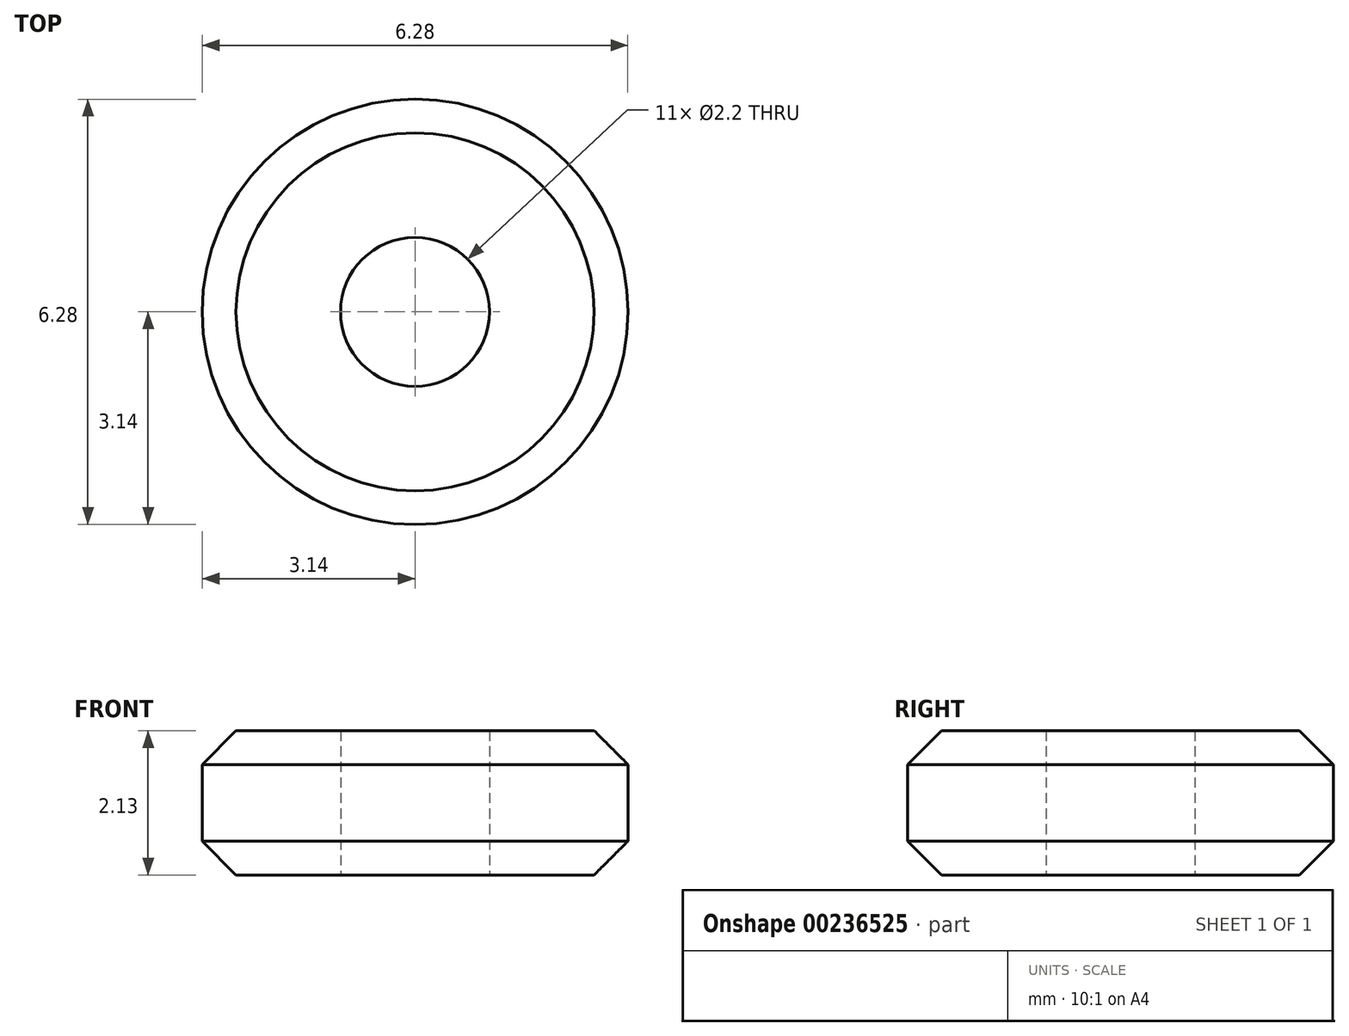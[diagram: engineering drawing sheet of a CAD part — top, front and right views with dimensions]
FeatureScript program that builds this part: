
annotation { "Feature Type Name" : "Feature", "Feature Type Description" : "" }
export const myFeature = defineFeature(function(context is Context, id is Id, definition is map)
    precondition{}
    {
        {
            assignVariable(context, id + "F0", {"name" : "scale", "anyValue" : 1 / 160});
        }
        {
            var Q0;
            Q0=qCreatedBy(makeId("Top.planeOp"),FACE);
            var sketch = newSketch(context, id + "F1", { "sketchPlane" : qUnion([Q0])});
            skCircle(sketch, "E0", {"center": v(0, 0) * mm, "radius": 3.14 * mm});
            skCircle(sketch, "E1", {"center": v(0, 0) * mm, "radius": 1.1 * mm});
            skSolve(sketch);
        }
        {
            var Q0;
            Q0=qSketchRegion(id+"F1",true);
            extrude(context, id + "F2", {"entities" : qUnion([Q0]), "depth" : 341 * getVariable(context, 'scale') * mm});
        }
        {
            var Q0;
            Q0=makeQuery(id+"F2.opExtrude","CAP_EDGE",EDGE,{"disambiguationData":[OSD([sQuery(id+"F1.wireOp",EDGE,"E0")])],"isStart":true});
            var Q1;
            Q1=makeQuery(id+"F2.opExtrude","CAP_EDGE",EDGE,{"disambiguationData":[OSD([sQuery(id+"F1.wireOp",EDGE,"E0")])],"isStart":false});
            chamfer(context, id + "F3", {"entities" : qUnion([Q0, Q1]), "width" : 0.5 * mm, "tangentPropagation" : true});
        }
    });
